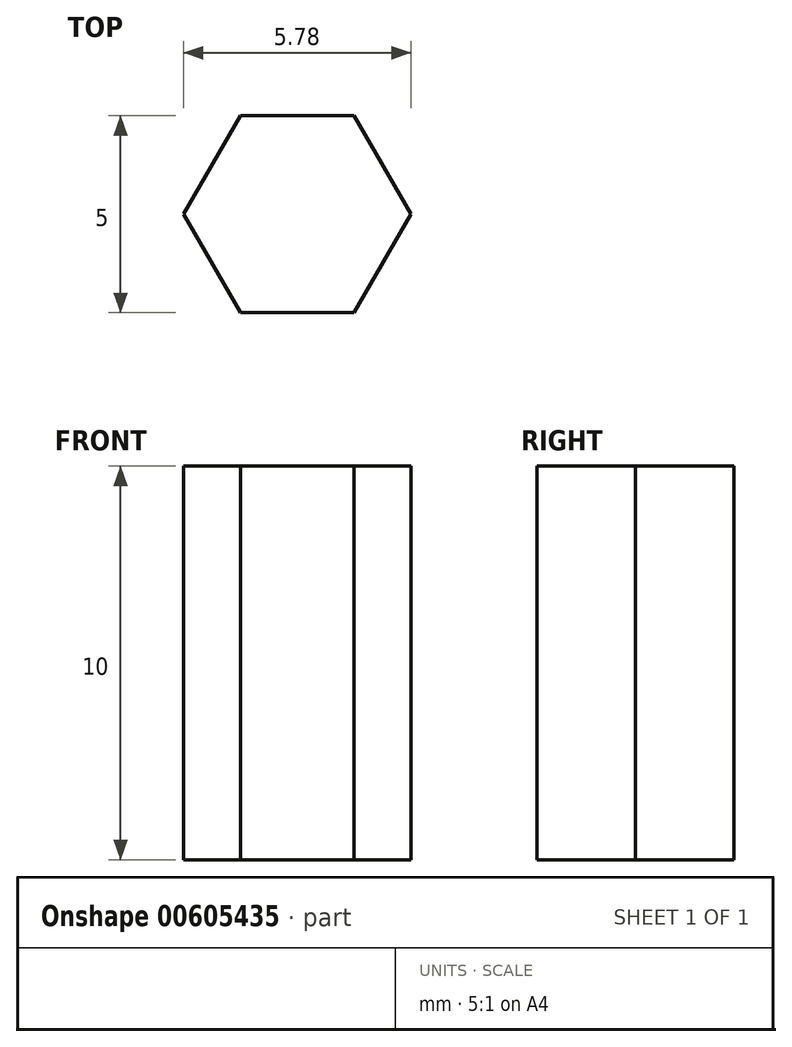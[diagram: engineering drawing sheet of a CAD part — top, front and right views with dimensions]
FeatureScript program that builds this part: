
annotation { "Feature Type Name" : "Feature", "Feature Type Description" : "" }
export const myFeature = defineFeature(function(context is Context, id is Id, definition is map)
    precondition{}
    {
        {
            var Q0;
            Q0=qCreatedBy(makeId("Top.planeOp"),FACE);
            var sketch = newSketch(context, id + "F0", { "sketchPlane" : qUnion([Q0])});
            skCircle(sketch, "E0.cCircle", {"center": v(0, 0) * mm, "radius": 2.5 * mm, "construction": true});
            skLineSegment(sketch, "E0.0", {"start": v(1.44, -2.5) * mm, "end": v(-1.44, -2.5) * mm});
            skLineSegment(sketch, "E0.1", {"start": v(-1.44, -2.5) * mm, "end": v(-2.89, 0) * mm});
            skLineSegment(sketch, "E0.2", {"start": v(-2.89, 0) * mm, "end": v(-1.44, 2.5) * mm});
            skLineSegment(sketch, "E0.3", {"start": v(-1.44, 2.5) * mm, "end": v(1.44, 2.5) * mm});
            skLineSegment(sketch, "E0.4", {"start": v(1.44, 2.5) * mm, "end": v(2.89, 0) * mm});
            skLineSegment(sketch, "E0.5", {"start": v(2.89, 0) * mm, "end": v(1.44, -2.5) * mm});
            skPoint(sketch, "E0.0.midPoint", {"position": v(0, -2.5) * mm});
            skSolve(sketch);
        }
        {
            var Q0;
            Q0 = qSketchRegion(id + "F0", true);
            var Q1;
            Q1=makeQuery(id+"F0.imprint","IMPRINT",FACE,{"disambiguationData":[TD([[makeQuery(id+"F0.imprint","IMPRINT",EDGE,{"derivedFrom":sQuery(id+"F0.wireOp",EDGE,"E0.0")}),-1.0]])]});
            extrude(context, id + "F1", {"entities" : qUnion([Q0, Q1]), "depth" : 10 * mm, "offsetDistance" : 25 * mm});
        }
    });
